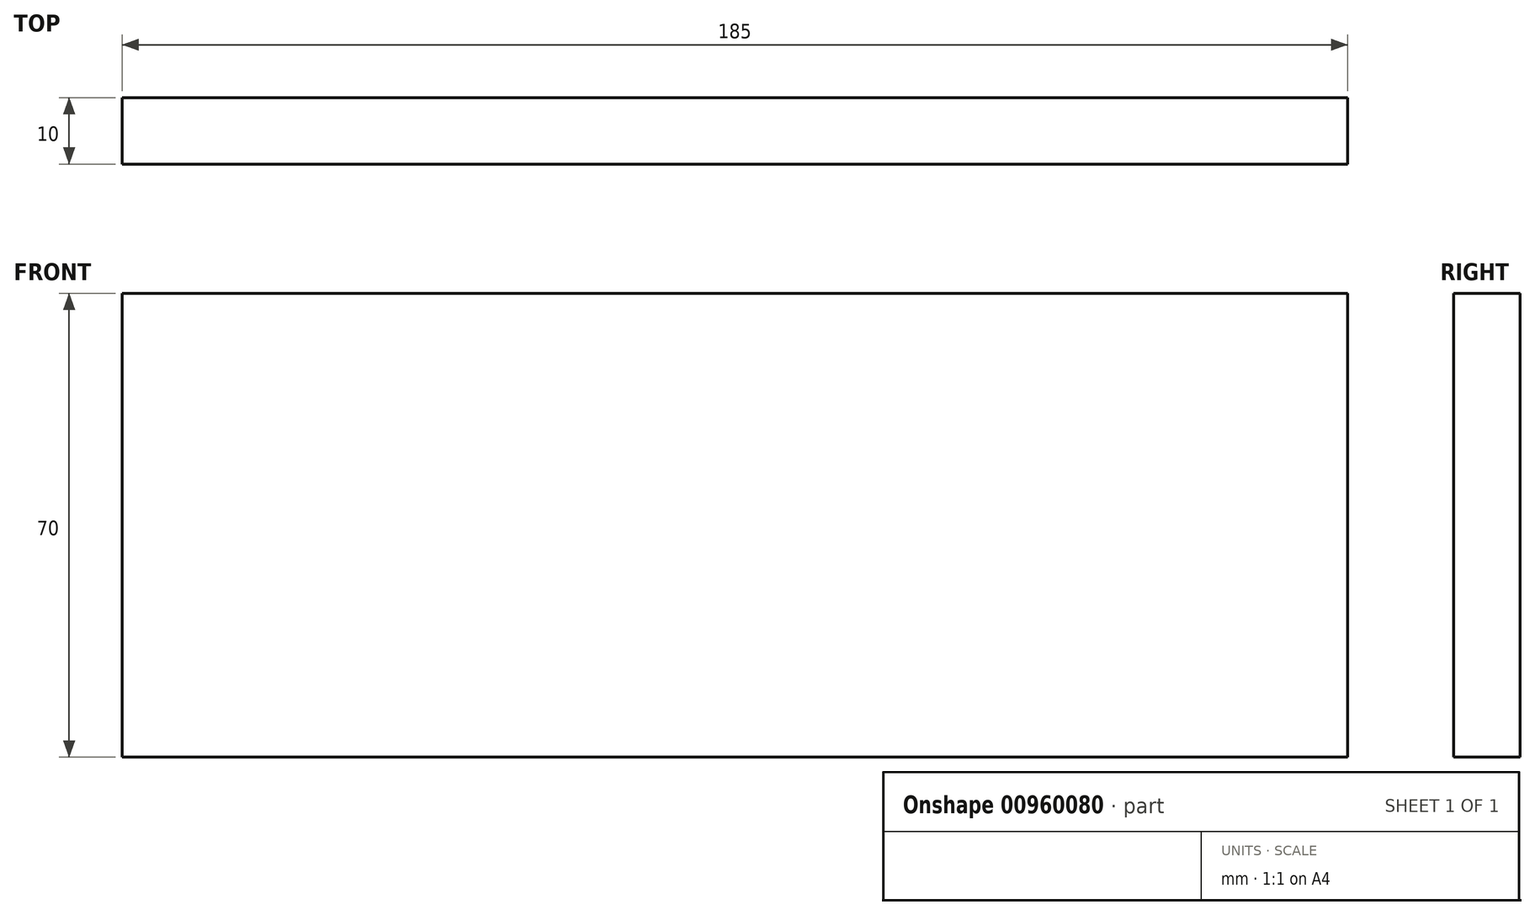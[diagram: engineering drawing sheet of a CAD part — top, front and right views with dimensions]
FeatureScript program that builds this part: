
annotation { "Feature Type Name" : "Feature", "Feature Type Description" : "" }
export const myFeature = defineFeature(function(context is Context, id is Id, definition is map)
    precondition{}
    {
        {
            var Q0;
            Q0=qCreatedBy(makeId("Front.planeOp"),FACE);
            var sketch = newSketch(context, id + "F0", { "sketchPlane" : qUnion([Q0])});
            skLineSegment(sketch, "E0.bottom", {"start": v(-92.5, 35) * mm, "end": v(92.5, 35) * mm});
            skLineSegment(sketch, "E0.top", {"start": v(-92.5, -35) * mm, "end": v(92.5, -35) * mm});
            skLineSegment(sketch, "E0.left", {"start": v(-92.5, 35) * mm, "end": v(-92.5, -35) * mm});
            skLineSegment(sketch, "E0.right", {"start": v(92.5, 35) * mm, "end": v(92.5, -35) * mm});
            skPoint(sketch, "E0.middle", {"position": v(0, 0) * mm});
            skSolve(sketch);
        }
        {
            var Q0;
            Q0=makeQuery(id+"F0.imprint","IMPRINT",FACE,{"disambiguationData":[TD([[makeQuery(id+"F0.imprint","IMPRINT",EDGE,{"derivedFrom":sQuery(id+"F0.wireOp",EDGE,"E0.bottom")}),-1.0]])]});
            extrude(context, id + "F1", {"entities" : qUnion([Q0]), "depth" : 10 * mm, "offsetDistance" : 25 * mm});
        }
    });
